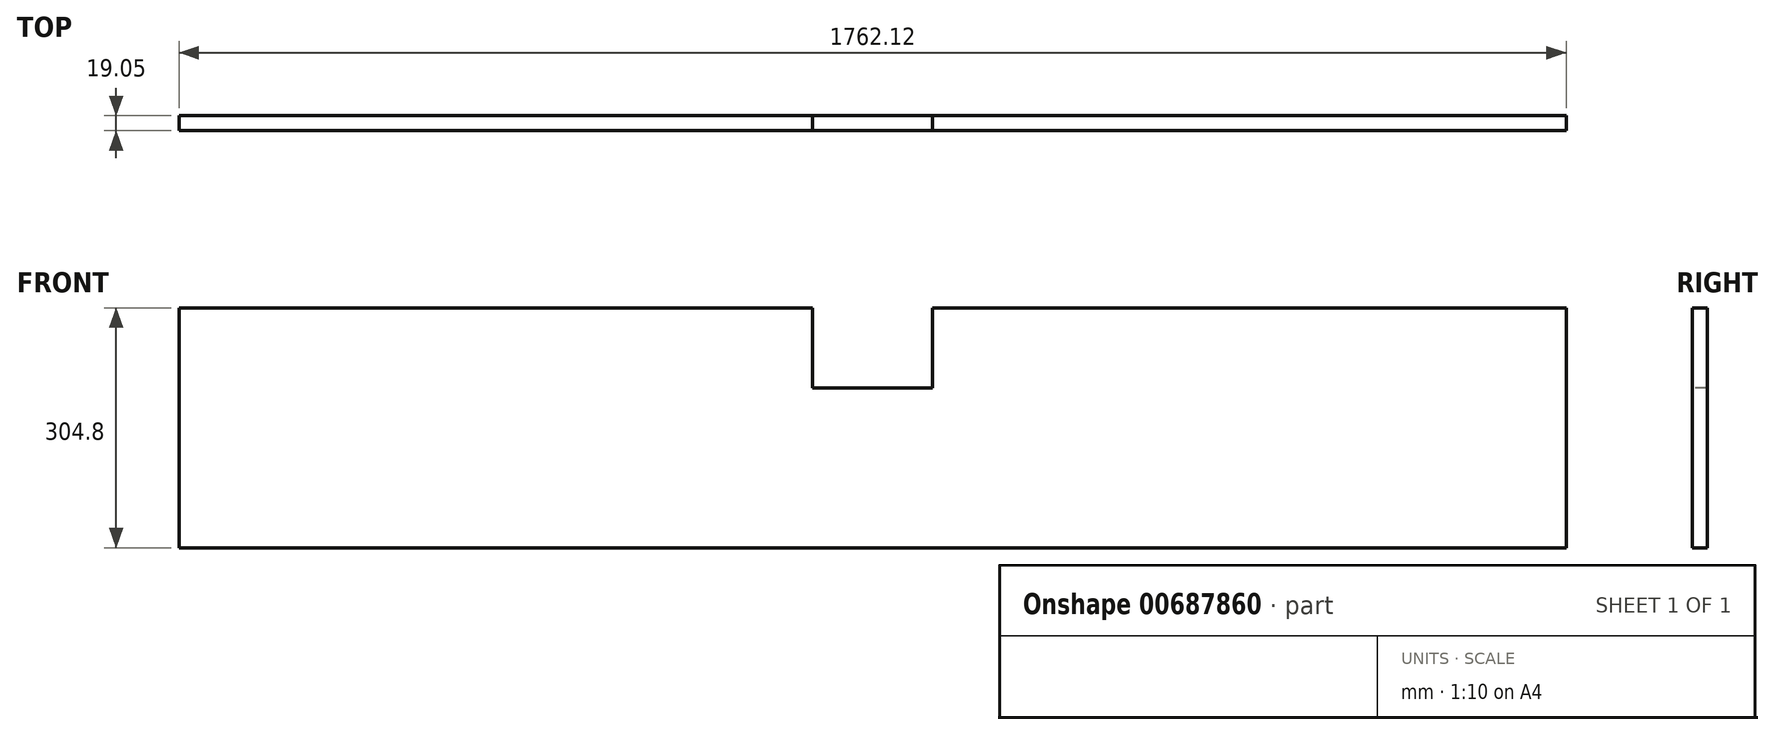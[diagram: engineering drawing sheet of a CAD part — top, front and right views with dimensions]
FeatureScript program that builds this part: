
annotation { "Feature Type Name" : "Feature", "Feature Type Description" : "" }
export const myFeature = defineFeature(function(context is Context, id is Id, definition is map)
    precondition{}
    {
        {
            var Q0;
            Q0=qCreatedBy(makeId("Front.planeOp"),FACE);
            var sketch = newSketch(context, id + "F0", { "sketchPlane" : qUnion([Q0])});
            skLineSegment(sketch, "E0.bottom", {"start": v(881.06, 152.4) * mm, "end": v(-881.06, 152.4) * mm});
            skLineSegment(sketch, "E0.top", {"start": v(881.06, -152.4) * mm, "end": v(-881.06, -152.4) * mm});
            skLineSegment(sketch, "E0.left", {"start": v(881.06, 152.4) * mm, "end": v(881.06, -152.4) * mm});
            skLineSegment(sketch, "E0.right", {"start": v(-881.06, 152.4) * mm, "end": v(-881.06, -152.4) * mm});
            skPoint(sketch, "E0.middle", {"position": v(0, 0) * mm});
            skSolve(sketch);
        }
        {
            var Q0;
            Q0=makeQuery(id+"F0.imprint","IMPRINT",FACE,{"disambiguationData":[TD([[makeQuery(id+"F0.imprint","IMPRINT",EDGE,{"derivedFrom":sQuery(id+"F0.wireOp",EDGE,"E0.bottom")}),1.0]])]});
            extrude(context, id + "F1", {"entities" : qUnion([Q0]), "depth" : 19.05 * mm, "offsetDistance" : 25.4 * mm});
        }
        {
            var Q0;
            Q0=makeQuery(id+"F1.opExtrude","CAP_FACE",FACE,{"disambiguationData":[OSD([sQuery(id+"F0.wireOp",EDGE,"E0.bottom"),sQuery(id+"F0.wireOp",EDGE,"E0.top"),sQuery(id+"F0.wireOp",EDGE,"E0.left"),sQuery(id+"F0.wireOp",EDGE,"E0.right")])],"isStart":false});
            var sketch = newSketch(context, id + "F2", { "sketchPlane" : qUnion([Q0])});
            skLineSegment(sketch, "E1.bottom", {"start": v(-76.2, 50.8) * mm, "end": v(76.2, 50.8) * mm});
            skLineSegment(sketch, "E1.top", {"start": v(-76.2, 254) * mm, "end": v(76.2, 254) * mm});
            skLineSegment(sketch, "E1.left", {"start": v(-76.2, 50.8) * mm, "end": v(-76.2, 254) * mm});
            skLineSegment(sketch, "E1.right", {"start": v(76.2, 50.8) * mm, "end": v(76.2, 254) * mm});
            skPoint(sketch, "E1.middle", {"position": v(0, 152.4) * mm});
            skSolve(sketch);
        }
        {
            var Q0;
            {var subQ0=sQuery(id+"F2.wireOp",EDGE,"E1.bottom");Q0=makeQuery(id+"F2.imprint","IMPRINT",FACE,{"disambiguationData":[TD([[makeQuery(id+"F2.imprint","IMPRINT",EDGE,{"derivedFrom":subQ0}),1.0]])]});}
            extrude(context, id + "F3", {"entities" : qUnion([Q0]), "operationType" : NewBodyOperationType.REMOVE, "oppositeDirection" : true, "depth" : 25.4 * mm, "offsetDistance" : 25.4 * mm});
        }
    });
